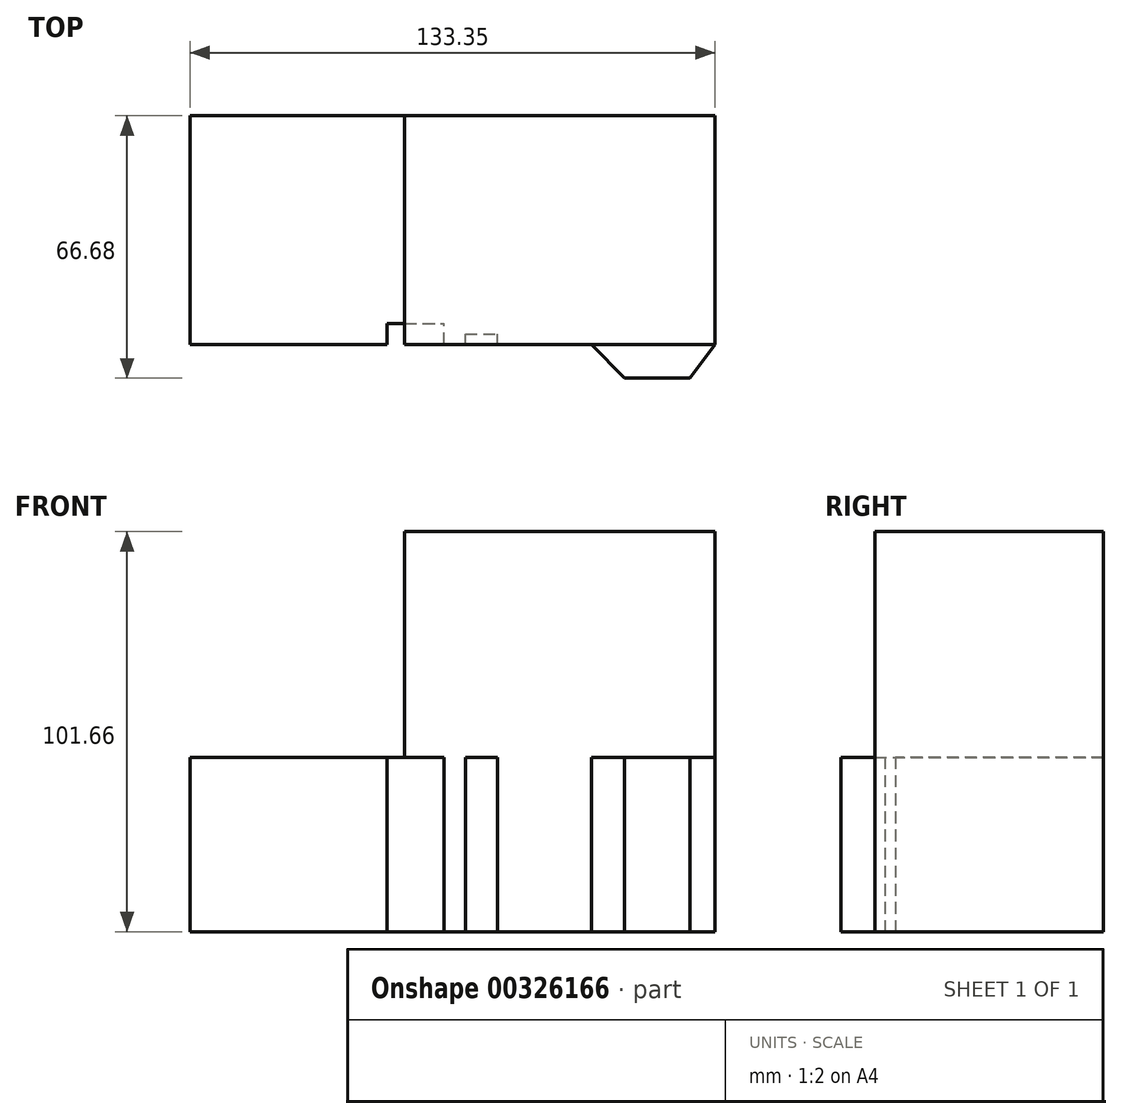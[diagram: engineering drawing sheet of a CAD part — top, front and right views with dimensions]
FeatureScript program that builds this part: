
annotation { "Feature Type Name" : "Feature", "Feature Type Description" : "" }
export const myFeature = defineFeature(function(context is Context, id is Id, definition is map)
    precondition{}
    {
        {
            var Q0;
            Q0=qCreatedBy(makeId("Top.planeOp"),FACE);
            var sketch = newSketch(context, id + "F0", { "sketchPlane" : qUnion([Q0])});
            skLineSegment(sketch, "E0", {"start": v(-64.48, 58.08) * mm, "end": v(68.87, 58.08) * mm});
            skLineSegment(sketch, "E1", {"start": v(68.87, 58.08) * mm, "end": v(68.87, 0) * mm});
            skLineSegment(sketch, "E2", {"start": v(62.5, -8.6) * mm, "end": v(45.82, -8.6) * mm});
            skLineSegment(sketch, "E3", {"start": v(45.82, -8.6) * mm, "end": v(37.49, 0) * mm});
            skLineSegment(sketch, "E4", {"start": v(37.49, 0) * mm, "end": v(0, 0) * mm});
            skLineSegment(sketch, "E5", {"start": v(0, 0) * mm, "end": v(-64.48, 0) * mm});
            skLineSegment(sketch, "E6", {"start": v(-64.48, 0) * mm, "end": v(-64.48, 58.08) * mm});
            skLineSegment(sketch, "E7", {"start": v(68.87, 0) * mm, "end": v(62.5, -8.6) * mm});
            skLineSegment(sketch, "E8.bottom", {"start": v(-14.48, 0) * mm, "end": v(0, 0) * mm});
            skLineSegment(sketch, "E8.top", {"start": v(-14.48, 5.28) * mm, "end": v(0, 5.28) * mm});
            skLineSegment(sketch, "E8.left", {"start": v(-14.48, 0) * mm, "end": v(-14.48, 5.28) * mm});
            skLineSegment(sketch, "E8.right", {"start": v(0, 0) * mm, "end": v(0, 5.28) * mm});
            skPoint(sketch, "E9.oppositeSnap0", {"position": v(0, 2.64) * mm});
            skLineSegment(sketch, "E9.bottom", {"start": v(5.46, 0) * mm, "end": v(13.64, 0) * mm});
            skLineSegment(sketch, "E9.top", {"start": v(5.46, 2.64) * mm, "end": v(13.64, 2.64) * mm});
            skLineSegment(sketch, "E9.left", {"start": v(5.46, 0) * mm, "end": v(5.46, 2.64) * mm});
            skLineSegment(sketch, "E9.right", {"start": v(13.64, 0) * mm, "end": v(13.64, 2.64) * mm});
            skSolve(sketch);
        }
        {
            var Q0;
            Q0=makeQuery(id+"F0.imprint","IMPRINT",FACE,{"disambiguationData":[TD([[makeQuery(id+"F0.imprint","IMPRINT",EDGE,{"derivedFrom":sQuery(id+"F0.wireOp",EDGE,"E0")}),-1.0]])]});
            extrude(context, id + "F1", {"entities" : qUnion([Q0]), "depth" : 44.36 * mm});
        }
        {
            var Q0;
            Q0=makeQuery(id+"F1.opExtrude","CAP_FACE",FACE,{"disambiguationData":[OSD([sQuery(id+"F0.wireOp",EDGE,"E0"),sQuery(id+"F0.wireOp",EDGE,"E2"),sQuery(id+"F0.wireOp",EDGE,"E3"),sQuery(id+"F0.wireOp",EDGE,"E4"),sQuery(id+"F0.wireOp",EDGE,"E5"),sQuery(id+"F0.wireOp",EDGE,"E6"),sQuery(id+"F0.wireOp",EDGE,"E1"),sQuery(id+"F0.wireOp",EDGE,"E7")])],"isStart":false});
            var sketch = newSketch(context, id + "F2", { "sketchPlane" : qUnion([Q0])});
            skLineSegment(sketch, "E10.bottom", {"start": v(-10.01, 58.08) * mm, "end": v(68.87, 58.08) * mm});
            skLineSegment(sketch, "E10.top", {"start": v(-10.01, 0) * mm, "end": v(68.87, 0) * mm});
            skLineSegment(sketch, "E10.left", {"start": v(-10.01, 58.08) * mm, "end": v(-10.01, 0) * mm});
            skLineSegment(sketch, "E10.right", {"start": v(68.87, 58.08) * mm, "end": v(68.87, 0) * mm});
            skSolve(sketch);
        }
        {
            var Q0;
            Q0 = qSketchRegion(id + "F2", true);
            extrude(context, id + "F3", {"entities" : qUnion([Q0]), "operationType" : NewBodyOperationType.ADD, "depth" : 57.3 * mm});
        }
    });
